# Revit family: Domotics-DomesticRanges-GEWISS-CHORUS_SIGNALLING-LAMP_1M
name_source: partatom
category: Apparecchi elettrici
revit_build: Autodesk Revit 2016 (Build: 20161004_0715(x64)
units: mm (PartAtom-declared; Revit-internal decimal feet)

## family parameters
Condiviso = Sì
Host = Superficie
Mantenere orientamento annotazione = Sì
Punto di calcolo locali = Sì
Quota connettore circolare = Usa diametro
Taglio con vuoti quando caricato = Sì
Tipo di parte = Normale

## types (1)
- Domotics-DomesticRanges-GEWISS-CHORUS_SIGNALLING-LAMP_1M
    Catalogue = DOMOTICS
    Catalogue Range = CHORUS - DOMESTIC RANGE
    Colore = Titanium
    Description. = Flat indicator lamp
    Descrizione = AMBER INDICATOR LAMP 1M TITANIUM
    EAN code = 8011564268500
    Electrocod = 0132
    GW - Colore diffusore = Amber
    GW - Significato colore = Attention
    GW - Unità di segnalazione = With wired lead
    IDF = 49d4496d-f6db-4e26-8ce7-55cd9d1ea79b
    IDT = fdc8d34e-45fe-4ab7-8fcf-fae2eb94421c
    Immagine tipo = GW14624.jpg
    Modello = GW14624
    N. moduli Chorus = 1
    No. Chorus modules: = 1
    Produttore = GEWISS S.p.A.
    Prospetto di default = 1219 mm
    SEO = Indicator
    Technical sheet = https://www.gewiss.com
    Tipo_ = Chorus Spie 1M_GENERICO : GW14624 Spia di segnalazione ambra 1M titanio
    URL = https://www.gewiss.com
    Version file RFA = 19.0

## geometry (parser evidence)
native form markers: Sweep x2
no freeform markers — native parametric forms only
